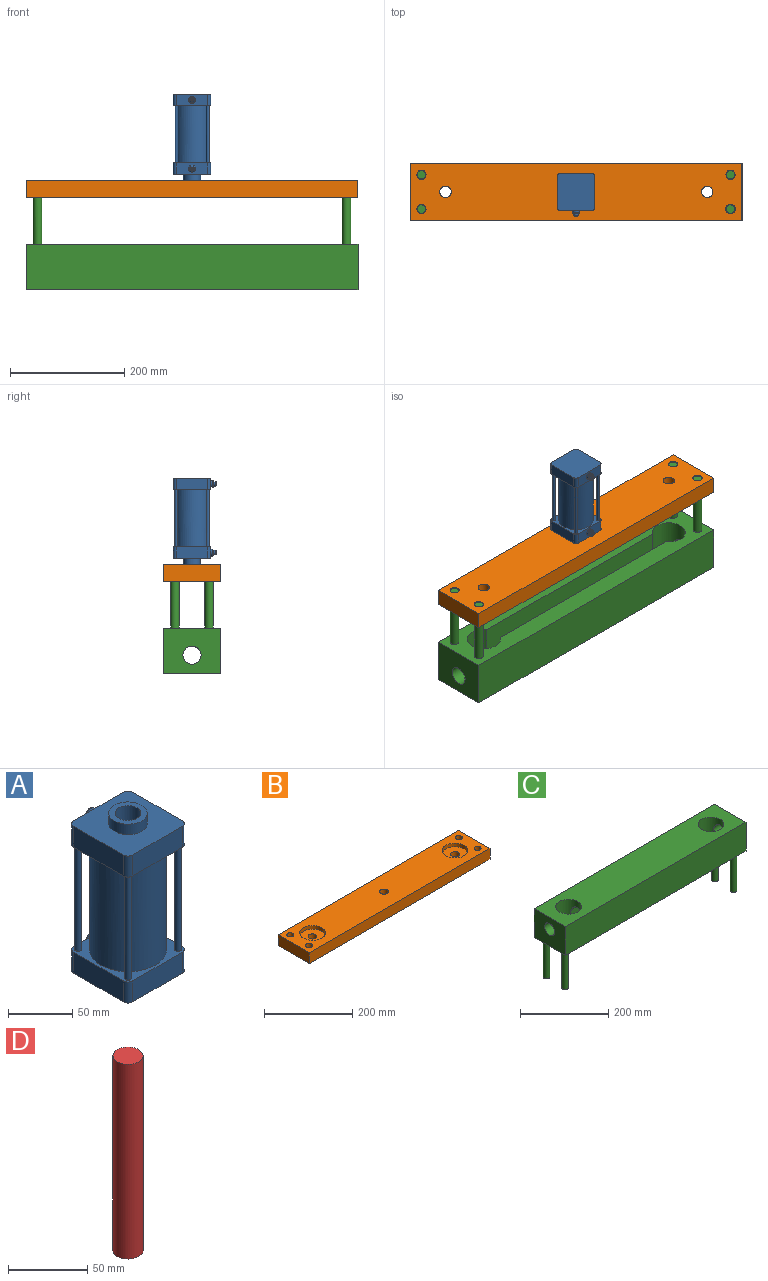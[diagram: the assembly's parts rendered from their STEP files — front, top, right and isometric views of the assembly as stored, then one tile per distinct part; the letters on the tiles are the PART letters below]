
ASSEMBLY  parts=4 mates=4
PART A: 47 faces, bbox 65x75x150 mm
  f0: plane 40x40mm, normal (0,0,1), area 1256.6mm2, adj f2
  f1: plane 40x40mm, normal (0,0,-1), area 942.5mm2, adj f2,f3
  f2: cylinder r=20mm len=100mm, axis (0,0,1), area 12566.4mm2, adj f0,f1
  f3: cylinder r=10mm len=30mm, axis (0,0,1), area 1885mm2, adj f1,f46
  f4: cylinder r=30mm len=100mm, axis (0,0,1), area 18849.6mm2, adj f13,f25
  f5: cylinder r=5mm len=20mm, axis (0,0,1), area 157.1mm2, adj f6,f12,f13,f14
  f6: plane 55x20mm, normal (0,-1,0), area 1100mm2, adj f5,f7,f13,f14
  f7: cylinder r=5mm len=20mm, axis (0,0,1), area 157.1mm2, adj f6,f8,f13,f14
  f8: plane 55x20mm, normal (-1,0,0), area 1100mm2, adj f7,f9,f13,f14
  f9: cylinder r=5mm len=20mm, axis (0,0,1), area 157.1mm2, adj f8,f10,f13,f14
  f10: plane 55x20mm, normal (0,1,0), area 986.9mm2, adj f9,f11,f13,f14,f16
  f11: cylinder r=5mm len=20mm, axis (0,0,1), area 157.1mm2, adj f10,f12,f13,f14
  f12: plane 55x20mm, normal (1,0,0), area 1100mm2, adj f5,f11,f13,f14
  f13: plane 65x65mm, normal (0,0,-1), area 1297.6mm2, adj f4,f5,f6,f7,f8,f9,f10,f11
  f14: plane 65x65mm, normal (0,0,1), area 3496.7mm2, adj f5,f6,f7,f8,f9,f10,f11,f12
  f15: plane 9x9mm, normal (0,1,0), area 13.4mm2, adj f34,f40
  f16: cylinder r=6mm len=12mm, axis (0,-1,0), area 131.9mm2, adj f10,f40
  f17: cylinder r=5mm len=20mm, axis (0,0,-1), area 157.1mm2, adj f18,f24,f25,f26
  f18: plane 55x20mm, normal (1,0,0), area 1100mm2, adj f17,f19,f25,f26
  f19: cylinder r=5mm len=20mm, axis (0,0,-1), area 157.1mm2, adj f18,f20,f25,f26
  f20: plane 55x20mm, normal (0,1,0), area 986.9mm2, adj f19,f21,f25,f26,f27
  f21: cylinder r=5mm len=20mm, axis (0,0,-1), area 157.1mm2, adj f20,f22,f25,f26
  f22: plane 55x20mm, normal (-1,0,0), area 1100mm2, adj f21,f23,f25,f26
  f23: cylinder r=5mm len=20mm, axis (0,0,-1), area 157.1mm2, adj f22,f24,f25,f26
  f24: plane 55x20mm, normal (0,-1,0), area 1100mm2, adj f17,f23,f25,f26
  f25: plane 65x65mm, normal (0,0,1), area 1297.6mm2, adj f4,f17,f18,f19,f20,f21,f22,f23
  f26: plane 65x65mm, normal (0,0,-1), area 4203.5mm2, adj f17,f18,f19,f20,f21,f22,f23,f24
  f27: cylinder r=6mm len=12mm, axis (0,-1,0), area 131.9mm2, adj f20,f38
  f28: plane 9x9mm, normal (0,1,0), area 13.4mm2, adj f30,f38
  f29: plane 5x5mm, normal (0,1,0), area 16.5mm2, adj f31,f37
  f30: cylinder r=4mm len=8mm, axis (0,-1,0), area 88mm2, adj f28,f37
  f31: cylinder r=1mm len=10mm, axis (0,-1,0), area 62.8mm2, adj f29,f32
  f32: plane 2x2mm, normal (0,1,0), area 3.1mm2, adj f31
  f33: plane 5x5mm, normal (0,1,0), area 16.5mm2, adj f35,f39
  f34: cylinder r=4mm len=8mm, axis (0,-1,0), area 88mm2, adj f15,f39
  f35: cylinder r=1mm len=10mm, axis (0,-1,0), area 62.8mm2, adj f33,f36
  f36: plane 2x2mm, normal (0,1,0), area 3.1mm2, adj f35
  f37: torus R=2.5mm, axis (0,1,0), area 51.1mm2, adj f29,f30
  f38: torus R=4.5mm, axis (0,1,0), area 80.8mm2, adj f27,f28
  f39: torus R=2.5mm, axis (0,1,0), area 51.1mm2, adj f33,f34
  f40: torus R=4.5mm, axis (0,1,0), area 80.8mm2, adj f15,f16
  f41: cylinder r=2.5mm len=100mm, axis (0,0,1), area 1570.8mm2, adj f13,f25
  f42: cylinder r=2.5mm len=100mm, axis (0,0,1), area 1570.8mm2, adj f13,f25
  f43: cylinder r=2.5mm len=100mm, axis (0,0,1), area 1570.8mm2, adj f13,f25
  f44: cylinder r=2.5mm len=100mm, axis (0,0,1), area 1570.8mm2, adj f13,f25
  f45: cylinder r=15mm len=30mm, axis (0,0,-1), area 942.5mm2, adj f14,f46
  f46: plane 30x30mm, normal (0,0,1), area 392.7mm2, adj f3,f45
PART B: 17 faces, bbox 580x100x30 mm
  f0: plane 100x30mm, normal (-1,0,0), area 3000mm2, adj f1,f5,f6,f9
  f1: plane 580x30mm, normal (0,-1,0), area 17400mm2, adj f0,f2,f6,f9
  f2: plane 100x30mm, normal (1,0,0), area 3000mm2, adj f1,f5,f6,f9
  f3: cylinder r=29mm len=58mm, axis (0,0,-1), area 1822.1mm2, adj f6,f7
  f4: cylinder r=29mm len=58mm, axis (0,0,-1), area 1822.1mm2, adj f6,f8
  f5: plane 580x30mm, normal (0,1,0), area 17400mm2, adj f0,f2,f6,f9
  f6: plane 580x100mm, normal (0,0,1), area 51582.1mm2, adj f0,f1,f2,f3,f4,f5,f12,f13
  f7: plane 58x58mm, normal (0,0,1), area 2327.9mm2, adj f3,f11
  f8: plane 58x58mm, normal (0,0,1), area 2327.9mm2, adj f4,f10
  f9: plane 580x100mm, normal (0,0,-1), area 56238mm2, adj f0,f1,f2,f5,f10,f11,f12,f13
  f10: cylinder r=10mm len=20mm, axis (0,0,1), area 1256.6mm2, adj f8,f9
  f11: cylinder r=10mm len=20mm, axis (0,0,1), area 1256.6mm2, adj f7,f9
  f12: cylinder r=8mm len=30mm, axis (0,0,1), area 1508mm2, adj f6,f9
  f13: cylinder r=8mm len=30mm, axis (0,0,1), area 1508mm2, adj f6,f9
  f14: cylinder r=8mm len=30mm, axis (0,0,1), area 1508mm2, adj f6,f9
  f15: cylinder r=8.3mm len=30mm, axis (0,0,1), area 1564.3mm2, adj f6,f9
  f16: cylinder r=10mm len=30mm, axis (0,0,1), area 1885mm2, adj f6,f9
PART C: 23 faces, bbox 580x100x190 mm
  f0: cylinder r=29mm len=80mm, axis (0,0,-1), area 11663.4mm2, adj f2,f7,f8,f10,f19,f20,f21,f22
  f1: cylinder r=29mm len=80mm, axis (0,0,-1), area 11662.8mm2, adj f2,f7,f8,f9,f19,f20,f21,f22
  f2: cylinder r=15.9mm len=408.44mm, axis (1,0,0), area 18120.9mm2, adj f0,f1,f19,f21
  f3: plane 100x80mm, normal (-1,0,0), area 7205.8mm2, adj f4,f6,f7,f8,f10
  f4: plane 580x80mm, normal (0,-1,0), area 46400mm2, adj f3,f5,f7,f8
  f5: plane 100x80mm, normal (1,0,0), area 7205.8mm2, adj f4,f6,f7,f8,f9
  f6: plane 580x80mm, normal (0,1,0), area 46400mm2, adj f3,f5,f7,f8
  f7: plane 580x100mm, normal (0,0,1), area 52715.8mm2, adj f0,f1,f3,f4,f5,f6
  f8: plane 580x100mm, normal (0,0,-1), area 38726.4mm2, adj f0,f1,f3,f4,f5,f6,f11,f13
  f9: cylinder r=15.9mm len=37.85mm, axis (1,0,0), area 3538.3mm2, adj f1,f5
  f10: cylinder r=15.9mm len=36.45mm, axis (1,0,0), area 3398.8mm2, adj f0,f3
  f11: cylinder r=7.5mm len=110mm, axis (0,0,1), area 5183.6mm2, adj f8,f12
  f12: plane 15x15mm, normal (0,0,-1), area 176.7mm2, adj f11
  f13: cylinder r=7.5mm len=110mm, axis (0,0,1), area 5183.6mm2, adj f8,f14
  f14: plane 15x15mm, normal (0,0,-1), area 176.7mm2, adj f13
  f15: cylinder r=7.5mm len=110mm, axis (0,0,1), area 5183.6mm2, adj f8,f16
  f16: plane 15x15mm, normal (0,0,-1), area 176.7mm2, adj f15
  f17: cylinder r=7.5mm len=110mm, axis (0,0,1), area 5183.6mm2, adj f8,f18
  f18: plane 15x15mm, normal (0,0,-1), area 176.7mm2, adj f17
  f19: plane 409.5x0.8mm, normal (0,0,-1), area 326.3mm2, adj f0,f1,f2,f20
  f20: plane 409.5x50mm, normal (0,1,0), area 20475.2mm2, adj f0,f1,f8,f19
  f21: plane 409.5x0.8mm, normal (0,0,-1), area 326.3mm2, adj f0,f1,f2,f22
  f22: plane 409.5x50mm, normal (0,-1,0), area 20475.2mm2, adj f0,f1,f8,f21
PART D: 3 faces, bbox 19x19x150 mm
  f0: cylinder r=9.5mm len=150mm, axis (0,0,-1), area 8953.5mm2, adj f1,f2
  f1: plane 19x19mm, normal (0,0,1), area 283.5mm2, adj f0
  f2: plane 19x19mm, normal (0,0,-1), area 283.5mm2, adj f0
PLACE A rot(axis=(1,0,0),180deg) t=(-109.23,104.39,365.68)mm
PLACE B rot(axis=(0,1,0),180deg) t=(-217.31,139.98,264.68)mm
PLACE C rot(axis=(0,-1,0),180deg) t=(-224.92,113.67,173.9)mm
PLACE D t=(-109.23,104.39,254.68)mm
MATE slider B.f16 <-> D.f0  axis (0,0,1) through (-109.23,104.39,284.68)mm
MATE slider D.f0 <-> A.f2  axis (0,0,1) through (-109.23,104.39,404.68)mm
MATE fastened B.f16 <-> D.f0  axis (0,0,-1) through (-109.23,104.39,254.68)mm
MATE slider B.f12 <-> C.f13  axis (0,0,-1) through (160.77,134.39,254.68)mm
